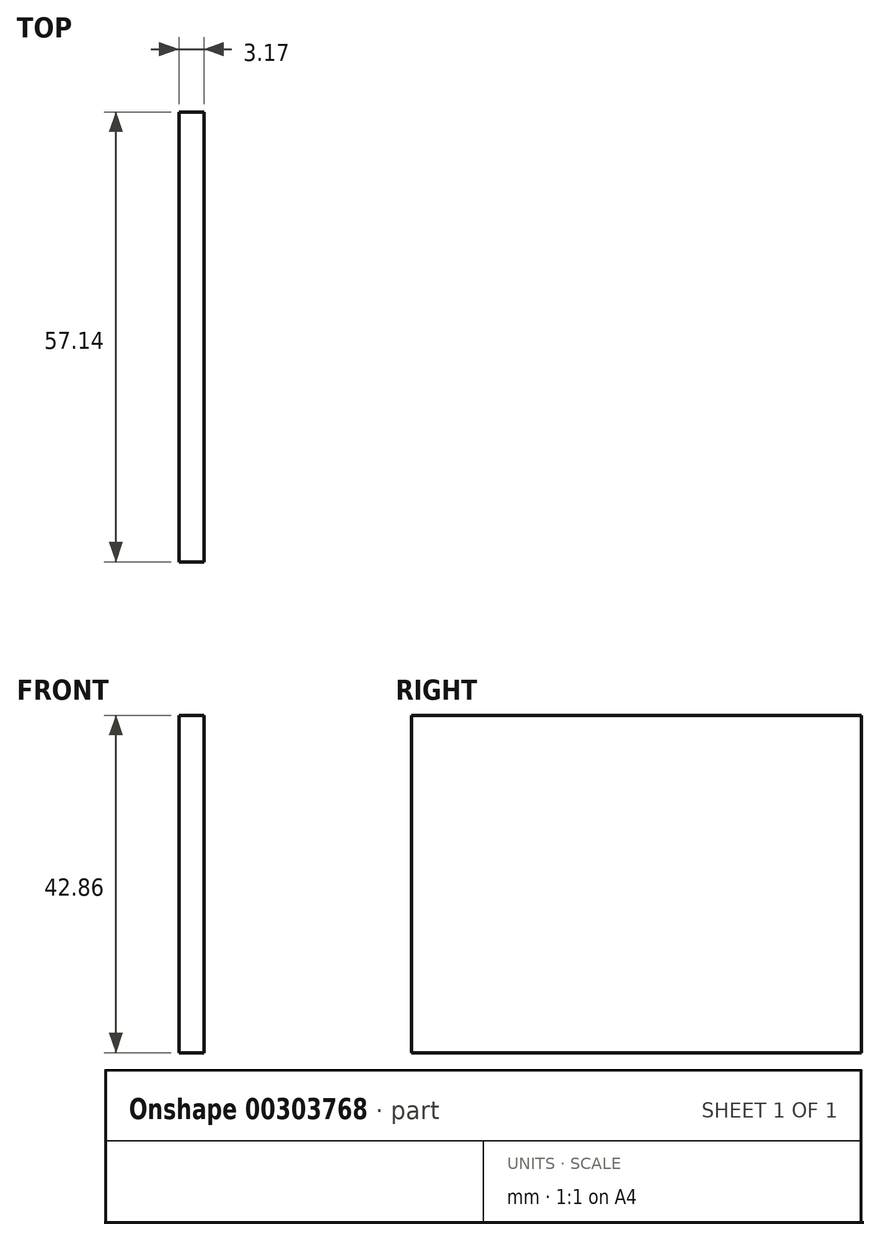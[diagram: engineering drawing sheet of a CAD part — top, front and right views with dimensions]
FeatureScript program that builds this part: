
annotation { "Feature Type Name" : "Feature", "Feature Type Description" : "" }
export const myFeature = defineFeature(function(context is Context, id is Id, definition is map)
    precondition{}
    {
        {
            var Q0;
            Q0=qCreatedBy(makeId("Right.planeOp"),FACE);
            var sketch = newSketch(context, id + "F0", { "sketchPlane" : qUnion([Q0])});
            skLineSegment(sketch, "E0.bottom", {"start": v(28.58, 21.43) * mm, "end": v(-28.58, 21.43) * mm});
            skLineSegment(sketch, "E0.top", {"start": v(28.58, -21.43) * mm, "end": v(-28.58, -21.43) * mm});
            skLineSegment(sketch, "E0.left", {"start": v(28.58, 21.43) * mm, "end": v(28.58, -21.43) * mm});
            skLineSegment(sketch, "E0.right", {"start": v(-28.58, 21.43) * mm, "end": v(-28.58, -21.43) * mm});
            skPoint(sketch, "E0.middle", {"position": v(0, 0) * mm});
            skSolve(sketch);
        }
        {
            var Q0;
            Q0=makeQuery(id+"F0.imprint","IMPRINT",FACE,{"disambiguationData":[TD([[makeQuery(id+"F0.imprint","IMPRINT",EDGE,{"derivedFrom":sQuery(id+"F0.wireOp",EDGE,"E0.bottom")}),1.0]])]});
            extrude(context, id + "F1", {"entities" : qUnion([Q0]), "depth" : 3.17 * mm});
        }
    });
